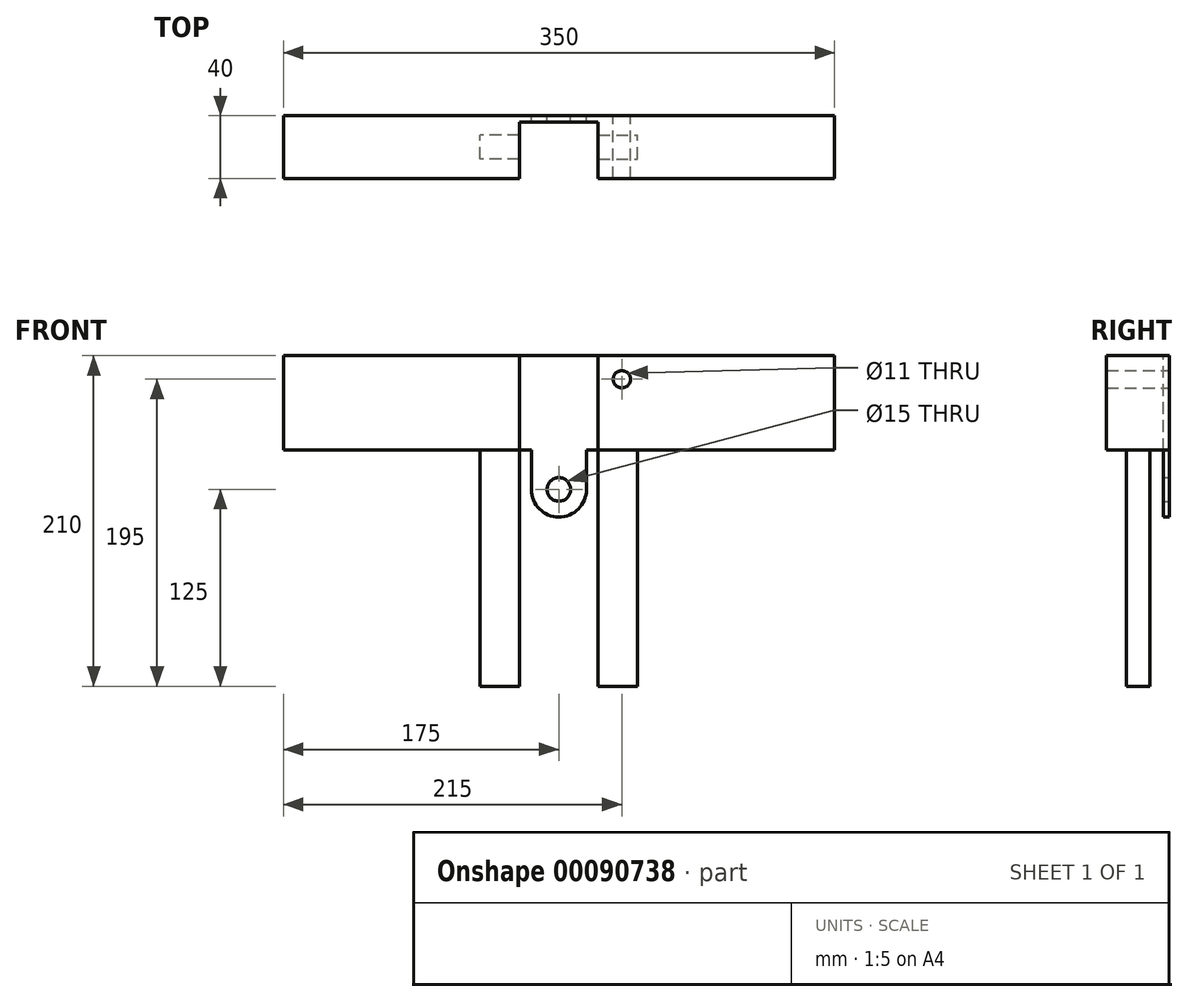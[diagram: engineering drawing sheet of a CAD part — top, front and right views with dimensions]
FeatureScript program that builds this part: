
annotation { "Feature Type Name" : "Feature", "Feature Type Description" : "" }
export const myFeature = defineFeature(function(context is Context, id is Id, definition is map)
    precondition{}
    {
        {
            var Q0;
            Q0=qCreatedBy(makeId("Front.planeOp"),FACE);
            var sketch = newSketch(context, id + "F0", { "sketchPlane" : qUnion([Q0])});
            skLineSegment(sketch, "E0.bottom", {"start": v(175, -30) * mm, "end": v(25, -30) * mm});
            skLineSegment(sketch, "E0.top", {"start": v(175, 30) * mm, "end": v(25, 30) * mm});
            skLineSegment(sketch, "E0.left", {"start": v(175, -30) * mm, "end": v(175, 30) * mm});
            skLineSegment(sketch, "E0.right", {"start": v(25, -30) * mm, "end": v(25, 30) * mm});
            skPoint(sketch, "E0.middle", {"position": v(100, 0) * mm});
            skLineSegment(sketch, "E1.bottom", {"start": v(-25, -30) * mm, "end": v(-175, -30) * mm});
            skLineSegment(sketch, "E1.top", {"start": v(-25, 30) * mm, "end": v(-175, 30) * mm});
            skLineSegment(sketch, "E1.left", {"start": v(-25, -30) * mm, "end": v(-25, 30) * mm});
            skLineSegment(sketch, "E1.right", {"start": v(-175, -30) * mm, "end": v(-175, 30) * mm});
            skPoint(sketch, "E1.middle", {"position": v(-100, 0) * mm});
            skLineSegment(sketch, "E2", {"start": v(-25, 0) * mm, "end": v(0, 0) * mm, "construction": true});
            skLineSegment(sketch, "E3", {"start": v(0, 0) * mm, "end": v(25, 0) * mm, "construction": true});
            skSolve(sketch);
        }
        {
            var Q0;
            Q0 = qSketchRegion(id + "F0", true);
            extrude(context, id + "F1", {"entities" : qUnion([Q0]), "endBound" : BoundingType.SYMMETRIC, "depth" : 40 * mm});
        }
        {
            var Q0;
            Q0=qCreatedBy(makeId("Front.planeOp"),FACE);
            var sketch = newSketch(context, id + "F2", { "sketchPlane" : qUnion([Q0])});
            skLineSegment(sketch, "E4.bottom", {"start": v(-25, -30) * mm, "end": v(-50, -30) * mm});
            skLineSegment(sketch, "E4.top", {"start": v(-25, -180) * mm, "end": v(-50, -180) * mm});
            skLineSegment(sketch, "E4.left", {"start": v(-25, -30) * mm, "end": v(-25, -180) * mm});
            skLineSegment(sketch, "E4.right", {"start": v(-50, -30) * mm, "end": v(-50, -180) * mm});
            skLineSegment(sketch, "E5.bottom", {"start": v(25, -30) * mm, "end": v(50, -30) * mm});
            skLineSegment(sketch, "E5.top", {"start": v(25, -180) * mm, "end": v(50, -180) * mm});
            skLineSegment(sketch, "E5.left", {"start": v(25, -30) * mm, "end": v(25, -180) * mm});
            skLineSegment(sketch, "E5.right", {"start": v(50, -30) * mm, "end": v(50, -180) * mm});
            skSolve(sketch);
        }
        {
            var Q0;
            Q0 = qSketchRegion(id + "F2", true);
            extrude(context, id + "F3", {"entities" : qUnion([Q0]), "operationType" : NewBodyOperationType.ADD, "endBound" : BoundingType.SYMMETRIC, "depth" : 15 * mm});
        }
        {
            var Q0;
            Q0=makeQuery(id+"F1.opExtrude","CAP_FACE",FACE,{"disambiguationData":[OSD([sQuery(id+"F0.wireOp",EDGE,"E1.bottom"),sQuery(id+"F0.wireOp",EDGE,"E1.top"),sQuery(id+"F0.wireOp",EDGE,"E1.left"),sQuery(id+"F0.wireOp",EDGE,"E1.right")])],"isStart":true});
            var sketch = newSketch(context, id + "F4", { "sketchPlane" : qUnion([Q0])});
            skLineSegment(sketch, "E6.bottom", {"start": v(17.5, 30) * mm, "end": v(-17.5, 30) * mm});
            skLineSegment(sketch, "E6.left", {"start": v(17.5, -30) * mm, "end": v(17.5, -55) * mm});
            skLineSegment(sketch, "E6.right", {"start": v(-17.5, 30) * mm, "end": v(-17.5, -55) * mm});
            skLineSegment(sketch, "E7.bottom", {"start": v(25, 30) * mm, "end": v(17.5, 30) * mm});
            skLineSegment(sketch, "E7.top", {"start": v(25, -30) * mm, "end": v(17.5, -30) * mm});
            skLineSegment(sketch, "E7.left", {"start": v(25, 30) * mm, "end": v(25, -30) * mm});
            skCircle(sketch, "E8", {"center": v(0, -55) * mm, "radius": 7.5 * mm});
            skCircle(sketch, "E9", {"center": v(0, -55) * mm, "radius": 17.5 * mm});
            skSolve(sketch);
        }
        {
            var Q0;
            Q0 = qSketchRegion(id + "F4", true);
            extrude(context, id + "F5", {"entities" : qUnion([Q0]), "operationType" : NewBodyOperationType.ADD, "oppositeDirection" : true, "depth" : 4 * mm});
        }
        {
            var Q0;
            Q0=makeQuery(id+"F1.opExtrude","CAP_FACE",FACE,{"disambiguationData":[OSD([sQuery(id+"F0.wireOp",EDGE,"E0.bottom"),sQuery(id+"F0.wireOp",EDGE,"E0.top"),sQuery(id+"F0.wireOp",EDGE,"E0.left"),sQuery(id+"F0.wireOp",EDGE,"E0.right")])],"isStart":true});
            var sketch = newSketch(context, id + "F6", { "sketchPlane" : qUnion([Q0])});
            skCircle(sketch, "E10", {"center": v(-40, 15) * mm, "radius": 5.5 * mm});
            skSolve(sketch);
        }
        {
            var Q0;
            Q0 = qSketchRegion(id + "F6", true);
            extrude(context, id + "F7", {"entities" : qUnion([Q0]), "operationType" : NewBodyOperationType.REMOVE, "endBound" : BoundingType.THROUGH_ALL, "oppositeDirection" : true, "depth" : 25 * mm});
        }
        {
            var Q0;
            Q0=makeQuery(id+"F1.opExtrude","CAP_FACE",FACE,{"disambiguationData":[OSD([sQuery(id+"F0.wireOp",EDGE,"E0.bottom"),sQuery(id+"F0.wireOp",EDGE,"E0.top"),sQuery(id+"F0.wireOp",EDGE,"E0.left"),sQuery(id+"F0.wireOp",EDGE,"E0.right")])],"isStart":true});
            var sketch = newSketch(context, id + "F8", { "sketchPlane" : qUnion([Q0])});
            skLineSegment(sketch, "E11.bottom", {"start": v(-25, 30) * mm, "end": v(-17.5, 30) * mm});
            skLineSegment(sketch, "E11.top", {"start": v(-25, -30) * mm, "end": v(-17.5, -30) * mm});
            skLineSegment(sketch, "E11.left", {"start": v(-25, 30) * mm, "end": v(-25, -30) * mm});
            skLineSegment(sketch, "E12.bottom", {"start": v(-17.5, 30) * mm, "end": v(17.5, 30) * mm});
            skLineSegment(sketch, "E12.left", {"start": v(-17.5, -30) * mm, "end": v(-17.5, -55) * mm});
            skLineSegment(sketch, "E12.right", {"start": v(17.5, 30) * mm, "end": v(17.5, -55) * mm});
            skCircle(sketch, "E13", {"center": v(0, -55) * mm, "radius": 7.5 * mm});
            skCircle(sketch, "E14", {"center": v(0, -55) * mm, "radius": 17.5 * mm});
            skSolve(sketch);
        }
        {
            var Q0;
            Q0=makeQuery(id+"F8.imprint","IMPRINT",FACE,{"disambiguationData":[TD([[makeQuery(id+"F8.imprint","IMPRINT",EDGE,{"derivedFrom":sQuery(id+"F8.wireOp",EDGE,"E11.bottom")}),-1.0]])]});
            var Q1;
            Q1=makeQuery(id+"F8.imprint","IMPRINT",FACE,{"disambiguationData":[TD([[makeQuery(id+"F8.imprint","IMPRINT",EDGE,{"derivedFrom":sQuery(id+"F8.wireOp",EDGE,"E13")}),-1.0]])]});
            extrude(context, id + "F9", {"entities" : qUnion([Q0, Q1]), "operationType" : NewBodyOperationType.ADD, "oppositeDirection" : true, "depth" : 4 * mm});
        }
    });
